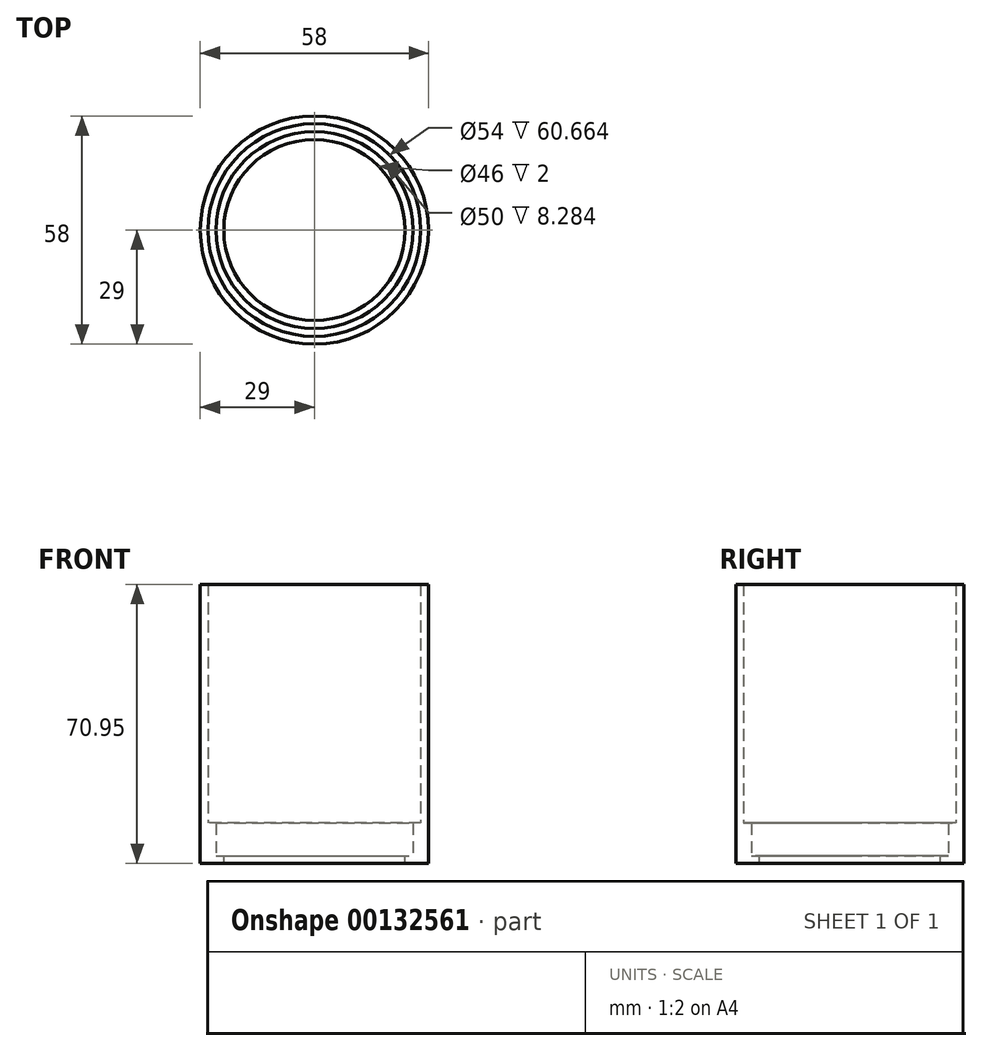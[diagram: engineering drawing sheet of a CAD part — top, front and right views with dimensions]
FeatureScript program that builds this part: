
annotation { "Feature Type Name" : "Feature", "Feature Type Description" : "" }
export const myFeature = defineFeature(function(context is Context, id is Id, definition is map)
    precondition{}
    {
        {
            var Q0;
            Q0=qCreatedBy(makeId("Top.planeOp"),FACE);
            var sketch = newSketch(context, id + "F0", { "sketchPlane" : qUnion([Q0])});
            skCircle(sketch, "E0", {"center": v(0, 0) * mm, "radius": 27 * mm});
            skSolve(sketch);
        }
        {
            var Q0;
            Q0=makeQuery(id+"F0.imprint","IMPRINT",FACE,{"disambiguationData":[TD([[makeQuery(id+"F0.imprint","IMPRINT",EDGE,{"derivedFrom":sQuery(id+"F0.wireOp",EDGE,"E0")}),1.0]])]});
            var sketch = newSketch(context, id + "F1", { "sketchPlane" : qUnion([Q0])});
            skCircle(sketch, "E1", {"center": v(0, 0) * mm, "radius": 29 * mm});
            skSolve(sketch);
        }
        {
            var Q0;
            Q0=makeQuery(id+"F1.imprint","IMPRINT",FACE,{"disambiguationData":[TD([[makeQuery(id+"F1.imprint","IMPRINT",EDGE,{"derivedFrom":sQuery(id+"F1.wireOp",EDGE,"E1")}),1.0]])]});
            extrude(context, id + "F2", {"entities" : qUnion([Q0]), "depth" : 68.95 * mm});
        }
        {
            var Q0;
            Q0=makeQuery(id+"F2.opExtrude","CAP_FACE",FACE,{"disambiguationData":[OSD([sQuery(id+"F0.wireOp",EDGE,"E0"),sQuery(id+"F1.wireOp",EDGE,"E1")])],"isStart":true});
            var sketch = newSketch(context, id + "F3", { "sketchPlane" : qUnion([Q0])});
            skCircle(sketch, "E2", {"center": v(0, 0) * mm, "radius": 25 * mm});
            skCircle(sketch, "E3", {"center": v(0, 0) * mm, "radius": 23 * mm});
            skSolve(sketch);
        }
        {
            var Q0;
            Q0=makeQuery(id+"F3.imprint","IMPRINT",FACE,{"disambiguationData":[TD([[makeQuery(id+"F3.imprint","IMPRINT",EDGE,{"derivedFrom":makeQuery(id+"F2.opExtrude","CAP_EDGE",EDGE,{"disambiguationData":[OSD([sQuery(id+"F1.wireOp",EDGE,"E1")])],"isStart":true})}),-1.0]])]});
            var Q1;
            Q1=makeQuery(id+"F3.imprint","IMPRINT",FACE,{"disambiguationData":[TD([[makeQuery(id+"F3.imprint","IMPRINT",EDGE,{"derivedFrom":sQuery(id+"F3.wireOp",EDGE,"E2")}),-1.0]])]});
            var Q2;
            Q2=makeQuery(id+"F3.imprint","IMPRINT",FACE,{"disambiguationData":[TD([[makeQuery(id+"F3.imprint","IMPRINT",EDGE,{"derivedFrom":sQuery(id+"F3.wireOp",EDGE,"E2")}),1.0]])]});
            extrude(context, id + "F4", {"entities" : qUnion([Q0, Q1, Q2]), "operationType" : NewBodyOperationType.ADD, "depth" : 2 * mm});
        }
        {
            var Q0;
            Q0=makeQuery(id+"F3.imprint","IMPRINT",FACE,{"disambiguationData":[TD([[makeQuery(id+"F3.imprint","IMPRINT",EDGE,{"derivedFrom":sQuery(id+"F3.wireOp",EDGE,"E2")}),-1.0]])]});
            extrude(context, id + "F5", {"entities" : qUnion([Q0]), "operationType" : NewBodyOperationType.ADD, "oppositeDirection" : true, "depth" : 8.28 * mm});
        }
    });
